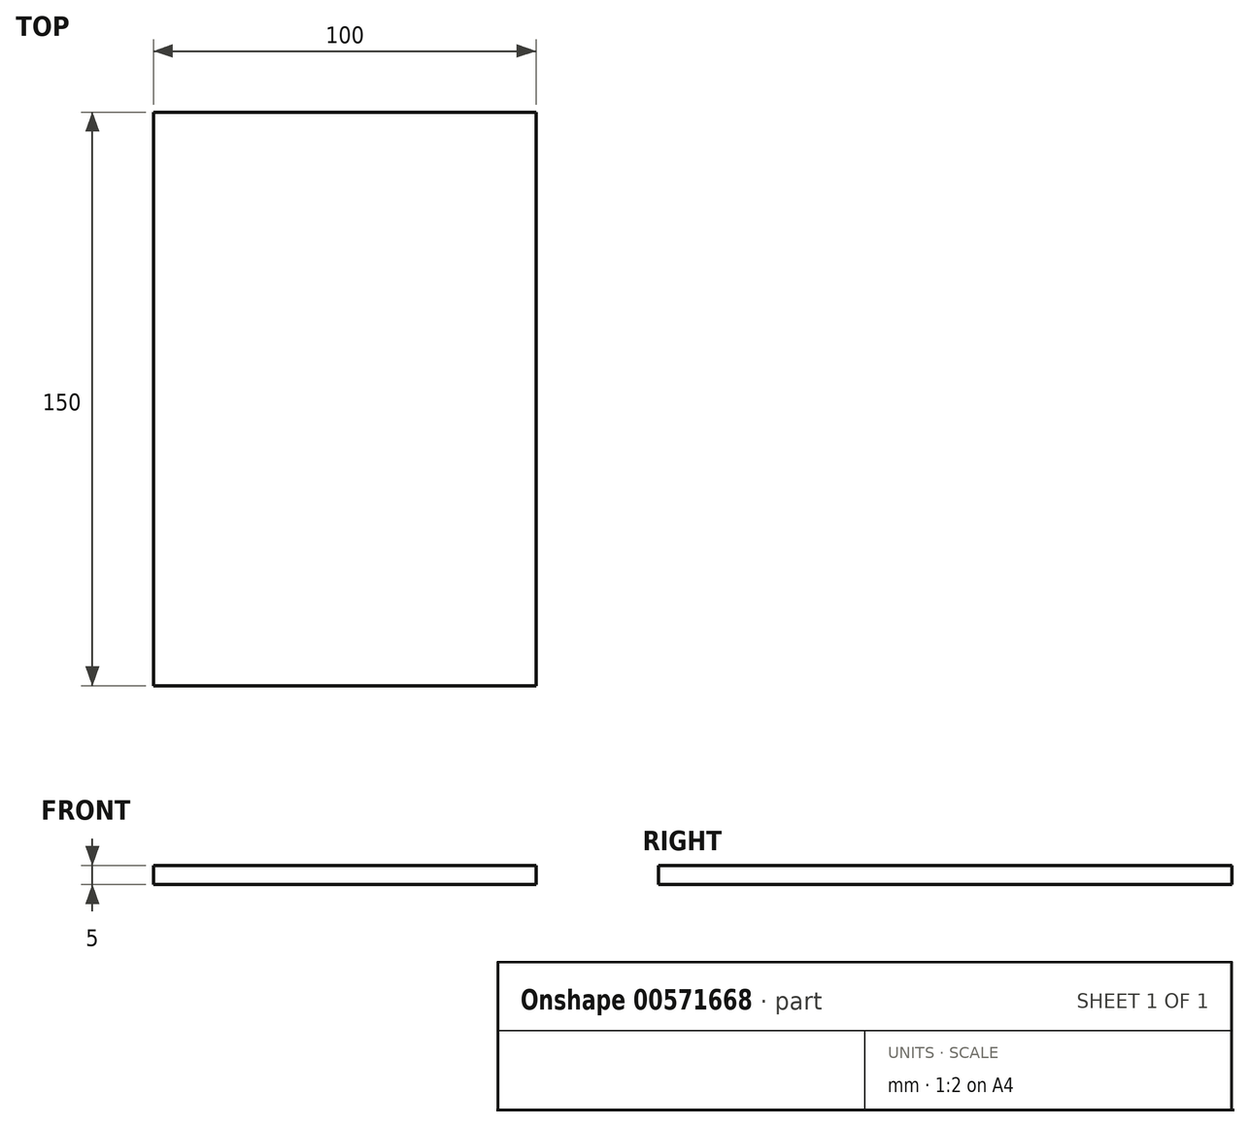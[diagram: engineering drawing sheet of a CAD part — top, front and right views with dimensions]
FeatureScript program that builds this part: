
annotation { "Feature Type Name" : "Feature", "Feature Type Description" : "" }
export const myFeature = defineFeature(function(context is Context, id is Id, definition is map)
    precondition{}
    {
        {
            var Q0;
            Q0=qCreatedBy(makeId("Top.planeOp"),FACE);
            var sketch = newSketch(context, id + "F0", { "sketchPlane" : qUnion([Q0])});
            skLineSegment(sketch, "E0.bottom", {"start": v(50, 75) * mm, "end": v(-50, 75) * mm});
            skLineSegment(sketch, "E0.top", {"start": v(50, -75) * mm, "end": v(-50, -75) * mm});
            skLineSegment(sketch, "E0.left", {"start": v(50, 75) * mm, "end": v(50, -75) * mm});
            skLineSegment(sketch, "E0.right", {"start": v(-50, 75) * mm, "end": v(-50, -75) * mm});
            skPoint(sketch, "E0.middle", {"position": v(0, 0) * mm});
            skSolve(sketch);
        }
        {
            var Q0;
            Q0 = qSketchRegion(id + "F0", true);
            extrude(context, id + "F1", {"entities" : qUnion([Q0]), "depth" : 5 * mm, "offsetDistance" : 25.4 * mm});
        }
    });
